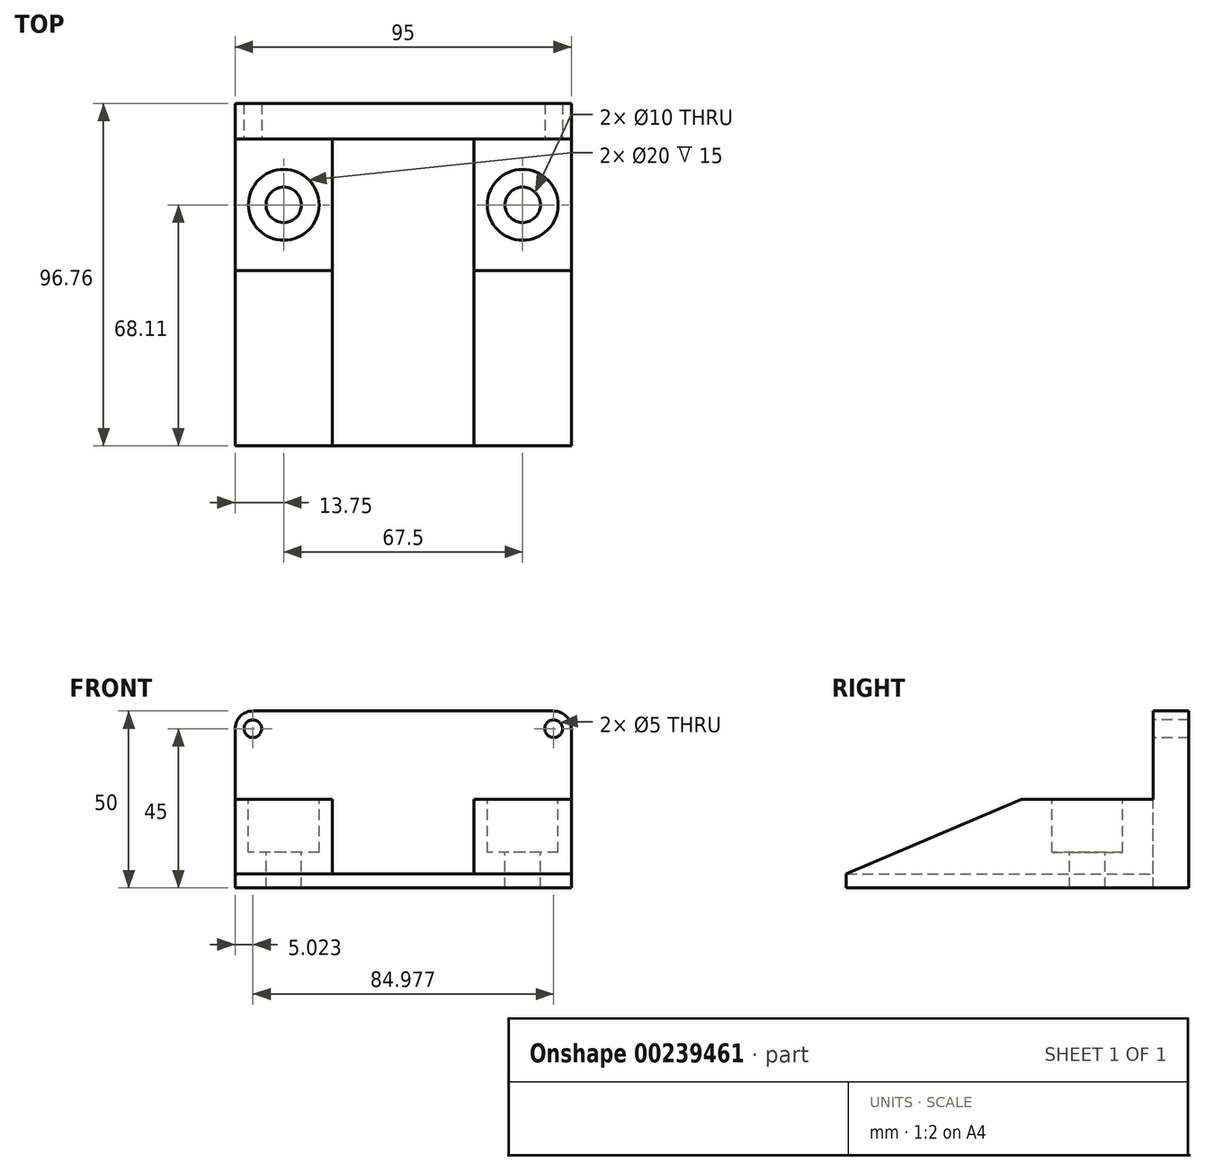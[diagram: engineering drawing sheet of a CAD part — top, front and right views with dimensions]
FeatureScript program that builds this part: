
annotation { "Feature Type Name" : "Feature", "Feature Type Description" : "" }
export const myFeature = defineFeature(function(context is Context, id is Id, definition is map)
    precondition{}
    {
        {
            var Q0;
            Q0=qCreatedBy(makeId("Top.planeOp"),FACE);
            var sketch = newSketch(context, id + "F0", { "sketchPlane" : qUnion([Q0])});
            skLineSegment(sketch, "E0.bottom", {"start": v(-20, -43.38) * mm, "end": v(20, -43.38) * mm});
            skLineSegment(sketch, "E0.top", {"start": v(-20, 43.38) * mm, "end": v(20, 43.38) * mm});
            skLineSegment(sketch, "E0.left", {"start": v(-20, -43.38) * mm, "end": v(-20, 43.38) * mm});
            skLineSegment(sketch, "E0.right", {"start": v(20, -43.38) * mm, "end": v(20, 43.38) * mm});
            skPoint(sketch, "E0.middle", {"position": v(0, 0) * mm});
            skSolve(sketch);
        }
        {
            var Q0;
            Q0=makeQuery(id+"F0.imprint","IMPRINT",FACE,{"disambiguationData":[TD([[makeQuery(id+"F0.imprint","IMPRINT",EDGE,{"derivedFrom":sQuery(id+"F0.wireOp",EDGE,"E0.bottom")}),1.0]])]});
            extrude(context, id + "F1", {"entities" : qUnion([Q0]), "depth" : 4 * mm});
        }
        {
            var Q0;
            Q0=makeQuery(id+"F1.opExtrude","SWEPT_FACE",FACE,{"disambiguationData":[OSD([sQuery(id+"F0.wireOp",EDGE,"E0.right")])]});
            var sketch = newSketch(context, id + "F2", { "sketchPlane" : qUnion([Q0])});
            skLineSegment(sketch, "E1.bottom", {"start": v(-43.38, 0) * mm, "end": v(51.62, 0) * mm});
            skLineSegment(sketch, "E1.top", {"start": v(-43.38, 25) * mm, "end": v(51.62, 25) * mm});
            skLineSegment(sketch, "E1.left", {"start": v(-43.38, 0) * mm, "end": v(-43.38, 25) * mm});
            skLineSegment(sketch, "E1.right", {"start": v(51.62, 0) * mm, "end": v(51.62, 25) * mm});
            skSolve(sketch);
        }
        {
            var Q0;
            Q0 = qSketchRegion(id + "F2", true);
            extrude(context, id + "F3", {"entities" : qUnion([Q0]), "operationType" : NewBodyOperationType.ADD, "depth" : 27.5 * mm});
        }
        {
            var Q0;
            Q0=makeQuery(id+"F1.opExtrude","SWEPT_FACE",FACE,{"disambiguationData":[OSD([sQuery(id+"F0.wireOp",EDGE,"E0.left")])]});
            var sketch = newSketch(context, id + "F4", { "sketchPlane" : qUnion([Q0])});
            skLineSegment(sketch, "E2.bottom", {"start": v(-43.38, 0) * mm, "end": v(43.38, 0) * mm});
            skLineSegment(sketch, "E2.top", {"start": v(-43.38, 25) * mm, "end": v(43.38, 25) * mm});
            skLineSegment(sketch, "E2.left", {"start": v(-43.38, 0) * mm, "end": v(-43.38, 25) * mm});
            skLineSegment(sketch, "E2.right", {"start": v(43.38, 0) * mm, "end": v(43.38, 25) * mm});
            skSolve(sketch);
        }
        {
            var Q0;
            Q0 = qSketchRegion(id + "F4", true);
            extrude(context, id + "F5", {"entities" : qUnion([Q0]), "operationType" : NewBodyOperationType.ADD, "depth" : 27.5 * mm});
        }
        {
            var Q0;
            Q0=makeQuery(id+"F5.boolean.opBoolean","MERGE",FACE,{"derivedFrom":[makeQuery(id+"F3.boolean.opBoolean","MERGE",FACE,{"derivedFrom":[makeQuery(id+"F1.opExtrude","SWEPT_FACE",FACE,{"disambiguationData":[OSD([sQuery(id+"F0.wireOp",EDGE,"E0.top")])]}),makeQuery(id+"F3.opExtrude","SWEPT_FACE",FACE,{"disambiguationData":[OSD([sQuery(id+"F2.wireOp",EDGE,"E1.right")])]})]}),makeQuery(id+"F5.opExtrude","SWEPT_FACE",FACE,{"disambiguationData":[OSD([sQuery(id+"F4.wireOp",EDGE,"E2.left")])]})]});
            var sketch = newSketch(context, id + "F6", { "sketchPlane" : qUnion([Q0])});
            skLineSegment(sketch, "E3.bottom", {"start": v(-47.5, 0) * mm, "end": v(47.48, 0) * mm});
            skLineSegment(sketch, "E3.top", {"start": v(-47.5, 50) * mm, "end": v(47.48, 50) * mm});
            skLineSegment(sketch, "E3.left", {"start": v(-47.5, 0) * mm, "end": v(-47.5, 50) * mm});
            skLineSegment(sketch, "E3.right", {"start": v(47.48, 0) * mm, "end": v(47.48, 50) * mm});
            skSolve(sketch);
        }
        {
            var Q0;
            Q0 = qSketchRegion(id + "F6", true);
            extrude(context, id + "F7", {"entities" : qUnion([Q0]), "operationType" : NewBodyOperationType.ADD, "depth" : 10 * mm});
        }
        {
            var Q0;
            Q0=makeQuery(id+"F5.opExtrude","CAP_FACE",FACE,{"disambiguationData":[OSD([sQuery(id+"F4.wireOp",EDGE,"E2.bottom"),sQuery(id+"F4.wireOp",EDGE,"E2.top"),sQuery(id+"F4.wireOp",EDGE,"E2.left"),sQuery(id+"F4.wireOp",EDGE,"E2.right")])],"isStart":false});
            var sketch = newSketch(context, id + "F8", { "sketchPlane" : qUnion([Q0])});
            skSolve(sketch);
        }
        {
            var Q0;
            Q0=makeQuery(id+"F7.opExtrude","SWEPT_EDGE",EDGE,{"disambiguationData":[OSD([sQuery(id+"F6.wireOp",EDGE,"E3.top"),sQuery(id+"F6.wireOp",EDGE,"E3.left")])]});
            fillet(context, id + "F9", {"entities" : qUnion([Q0]), "radius" : 5 * mm, "tangentPropagation" : true, "allowEdgeOverflow" : false});
        }
        {
            var Q0;
            Q0=makeQuery(id+"F7.opExtrude","SWEPT_EDGE",EDGE,{"disambiguationData":[OSD([sQuery(id+"F6.wireOp",EDGE,"E3.top"),sQuery(id+"F6.wireOp",EDGE,"E3.right")])]});
            fillet(context, id + "F10", {"entities" : qUnion([Q0]), "radius" : 5 * mm, "tangentPropagation" : true, "allowEdgeOverflow" : false});
        }
        {
            var Q0;
            Q0=makeQuery(id+"F7.opExtrude","CAP_FACE",FACE,{"disambiguationData":[OSD([sQuery(id+"F6.wireOp",EDGE,"E3.bottom"),sQuery(id+"F6.wireOp",EDGE,"E3.top"),sQuery(id+"F6.wireOp",EDGE,"E3.left"),sQuery(id+"F6.wireOp",EDGE,"E3.right")])],"isStart":true});
            var sketch = newSketch(context, id + "F11", { "sketchPlane" : qUnion([Q0])});
            skCircle(sketch, "E4", {"center": v(-42.48, 45) * mm, "radius": 2.5 * mm});
            skCircle(sketch, "E5", {"center": v(42.5, 45) * mm, "radius": 2.5 * mm});
            skSolve(sketch);
        }
        {
            var Q0;
            Q0 = qSketchRegion(id + "F11", true);
            extrude(context, id + "F12", {"entities" : qUnion([Q0]), "operationType" : NewBodyOperationType.REMOVE, "endBound" : BoundingType.THROUGH_ALL, "oppositeDirection" : true, "depth" : 25 * mm});
        }
        {
            var Q0;
            Q0=makeQuery(id+"F8.imprint","IMPRINT",FACE,{"disambiguationData":[TD([[makeQuery(id+"F8.imprint","IMPRINT",EDGE,{"derivedFrom":makeQuery(id+"F5.opExtrude","CAP_EDGE",EDGE,{"disambiguationData":[OSD([sQuery(id+"F4.wireOp",EDGE,"E2.bottom")])],"isStart":false})}),-1.0]])]});
            var sketch = newSketch(context, id + "F13", { "sketchPlane" : qUnion([Q0])});
            skLineSegment(sketch, "E6.0", {"start": v(-43.38, 25) * mm, "end": v(43.38, 25) * mm});
            skLineSegment(sketch, "E7.0", {"start": v(43.38, 25) * mm, "end": v(43.38, 4) * mm});
            skLineSegment(sketch, "E8", {"start": v(-6.08, 25) * mm, "end": v(43.38, 4) * mm});
            skPoint(sketch, "E9.orphan", {"position": v(43.38, 0) * mm});
            skSolve(sketch);
        }
        {
            var Q0;
            Q0 = qSketchRegion(id + "F13", true);
            extrude(context, id + "F14", {"entities" : qUnion([Q0]), "operationType" : NewBodyOperationType.REMOVE, "endBound" : BoundingType.THROUGH_ALL, "oppositeDirection" : true, "depth" : 25 * mm});
        }
        {
            var Q0;
            Q0=makeQuery(id+"F5.opExtrude","SWEPT_FACE",FACE,{"disambiguationData":[OSD([sQuery(id+"F4.wireOp",EDGE,"E2.top")])]});
            var sketch = newSketch(context, id + "F15", { "sketchPlane" : qUnion([Q0])});
            skPoint(sketch, "E10", {"position": v(-33.75, 24.73) * mm});
            skPoint(sketch, "E10.positionSnap0", {"position": v(-33.75, 6.08) * mm});
            skPoint(sketch, "E10.positionSnap1", {"position": v(-47.5, 24.73) * mm});
            skPoint(sketch, "E11.MirrorP", {"position": v(33.75, 24.73) * mm});
            skSolve(sketch);
        }
        {
            var Q0;
            Q0=sQuery(id+"F15.wireOp",VERTEX,"E10");
            var Q1;
            Q1=makeQuery(id+"F1.opExtrude","SWEPT_BODY",BODY,{"disambiguationData":[OSD([sQuery(id+"F0.wireOp",EDGE,"E0.bottom"),sQuery(id+"F0.wireOp",EDGE,"E0.top"),sQuery(id+"F0.wireOp",EDGE,"E0.left"),sQuery(id+"F0.wireOp",EDGE,"E0.right")])]});
            hole(context, id + "F16", {"style" : HoleStyle.C_BORE, "endStyle" : HoleEndStyle.THROUGH, "holeDiameter" : 10 * mm, "cBoreDiameter" : 20 * mm, "cBoreDepth" : 15 * mm, "locations" : qUnion([Q0]), "scope" : qUnion([Q1]), "isTappedThrough" : true});
        }
        {
            var Q0;
            Q0=sQuery(id+"F15.wireOp",VERTEX,"E11.MirrorP");
            var Q1;
            Q1=makeQuery(id+"F1.opExtrude","SWEPT_BODY",BODY,{"disambiguationData":[OSD([sQuery(id+"F0.wireOp",EDGE,"E0.bottom"),sQuery(id+"F0.wireOp",EDGE,"E0.top"),sQuery(id+"F0.wireOp",EDGE,"E0.left"),sQuery(id+"F0.wireOp",EDGE,"E0.right")])]});
            hole(context, id + "F17", {"style" : HoleStyle.C_BORE, "endStyle" : HoleEndStyle.THROUGH, "holeDiameter" : 10 * mm, "cBoreDiameter" : 20 * mm, "cBoreDepth" : 15 * mm, "locations" : qUnion([Q0]), "scope" : qUnion([Q1]), "isTappedThrough" : true});
        }
    });
